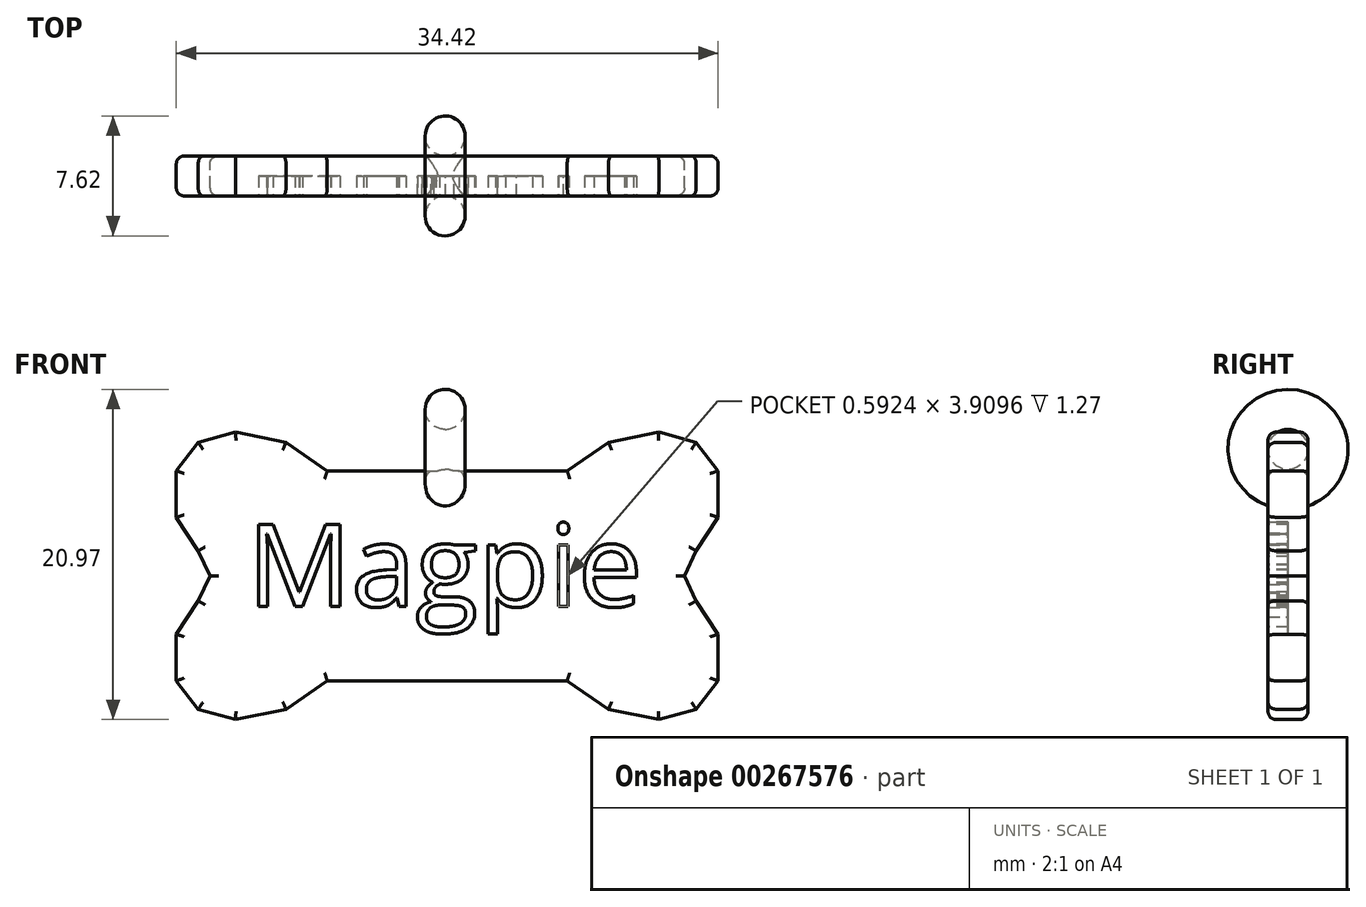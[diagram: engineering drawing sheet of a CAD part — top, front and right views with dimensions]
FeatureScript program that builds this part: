
annotation { "Feature Type Name" : "Feature", "Feature Type Description" : "" }
export const myFeature = defineFeature(function(context is Context, id is Id, definition is map)
    precondition{}
    {
        {
            var Q0;
            Q0=qCreatedBy(makeId("Front.planeOp"),FACE);
            var sketch = newSketch(context, id + "F0", { "sketchPlane" : qUnion([Q0])});
            skLineSegment(sketch, "E0", {"start": v(-5.6, 6.67) * mm, "end": v(2.01, 6.67) * mm});
            skLineSegment(sketch, "E1", {"start": v(2.01, 6.67) * mm, "end": v(4.63, 8.47) * mm});
            skLineSegment(sketch, "E2", {"start": v(4.63, 8.47) * mm, "end": v(7.83, 9.13) * mm});
            skLineSegment(sketch, "E3", {"start": v(7.83, 9.13) * mm, "end": v(10.2, 8.47) * mm});
            skLineSegment(sketch, "E4", {"start": v(10.2, 8.47) * mm, "end": v(11.6, 6.67) * mm});
            skLineSegment(sketch, "E5", {"start": v(11.6, 6.67) * mm, "end": v(11.6, 3.72) * mm});
            skLineSegment(sketch, "E6", {"start": v(11.6, 3.72) * mm, "end": v(10.2, 1.59) * mm});
            skLineSegment(sketch, "E7.MirrorCS", {"start": v(-5.6, 6.67) * mm, "end": v(-13.23, 6.67) * mm});
            skLineSegment(sketch, "E8.MirrorCS", {"start": v(-13.23, 6.67) * mm, "end": v(-15.85, 8.47) * mm});
            skLineSegment(sketch, "E9.MirrorCS", {"start": v(-15.85, 8.47) * mm, "end": v(-19.05, 9.13) * mm});
            skLineSegment(sketch, "E10.MirrorCS", {"start": v(-19.05, 9.13) * mm, "end": v(-21.42, 8.47) * mm});
            skLineSegment(sketch, "E11.MirrorCS", {"start": v(-21.42, 8.47) * mm, "end": v(-22.82, 6.67) * mm});
            skLineSegment(sketch, "E12.MirrorCS", {"start": v(-22.82, 6.67) * mm, "end": v(-22.82, 3.72) * mm});
            skLineSegment(sketch, "E13.MirrorCS", {"start": v(-22.82, 3.72) * mm, "end": v(-21.42, 1.59) * mm});
            skLineSegment(sketch, "E14.MirrorCS", {"start": v(11.6, -3.72) * mm, "end": v(10.2, -1.59) * mm});
            skLineSegment(sketch, "E15.MirrorCS", {"start": v(11.6, -6.67) * mm, "end": v(11.6, -3.72) * mm});
            skLineSegment(sketch, "E16.MirrorCS", {"start": v(10.2, -8.47) * mm, "end": v(11.6, -6.67) * mm});
            skLineSegment(sketch, "E17.MirrorCS", {"start": v(7.83, -9.13) * mm, "end": v(10.2, -8.47) * mm});
            skLineSegment(sketch, "E18.MirrorCS", {"start": v(4.63, -8.47) * mm, "end": v(7.83, -9.13) * mm});
            skLineSegment(sketch, "E19.MirrorCS", {"start": v(2.01, -6.67) * mm, "end": v(4.63, -8.47) * mm});
            skLineSegment(sketch, "E20.MirrorCS", {"start": v(-5.6, -6.67) * mm, "end": v(2.01, -6.67) * mm});
            skLineSegment(sketch, "E21.MirrorCS", {"start": v(-22.82, -3.72) * mm, "end": v(-21.42, -1.59) * mm});
            skLineSegment(sketch, "E22.MirrorCS", {"start": v(-22.82, -6.67) * mm, "end": v(-22.82, -3.72) * mm});
            skLineSegment(sketch, "E23.MirrorCS", {"start": v(-21.42, -8.47) * mm, "end": v(-22.82, -6.67) * mm});
            skLineSegment(sketch, "E24.MirrorCS", {"start": v(-19.05, -9.13) * mm, "end": v(-21.42, -8.47) * mm});
            skLineSegment(sketch, "E25.MirrorCS", {"start": v(-15.85, -8.47) * mm, "end": v(-19.05, -9.13) * mm});
            skLineSegment(sketch, "E26.MirrorCS", {"start": v(-13.23, -6.67) * mm, "end": v(-15.85, -8.47) * mm});
            skLineSegment(sketch, "E27.MirrorCS", {"start": v(-5.6, -6.67) * mm, "end": v(-13.23, -6.67) * mm});
            skLineSegment(sketch, "E28", {"start": v(10.2, 1.59) * mm, "end": v(9.47, 0) * mm});
            skLineSegment(sketch, "E29", {"start": v(9.47, 0) * mm, "end": v(10.2, -1.59) * mm});
            skLineSegment(sketch, "E30.MirrorCS", {"start": v(-21.42, 1.59) * mm, "end": v(-20.69, 0) * mm});
            skLineSegment(sketch, "E31.MirrorCS", {"start": v(-20.69, 0) * mm, "end": v(-21.42, -1.59) * mm});
            skSolve(sketch);
        }
        {
            var Q0;
            Q0 = qSketchRegion(id + "F0", true);
            extrude(context, id + "F1", {"entities" : qUnion([Q0]), "depth" : 2.54 * mm});
        }
        {
            var Q0;
            Q0=makeQuery(id+"F1.opExtrude","CAP_FACE",FACE,{"disambiguationData":[OSD([sQuery(id+"F0.wireOp",EDGE,"E0"),sQuery(id+"F0.wireOp",EDGE,"E1"),sQuery(id+"F0.wireOp",EDGE,"E2"),sQuery(id+"F0.wireOp",EDGE,"E3"),sQuery(id+"F0.wireOp",EDGE,"E4"),sQuery(id+"F0.wireOp",EDGE,"E5"),sQuery(id+"F0.wireOp",EDGE,"E6"),sQuery(id+"F0.wireOp",EDGE,"E7.MirrorCS"),sQuery(id+"F0.wireOp",EDGE,"E8.MirrorCS"),sQuery(id+"F0.wireOp",EDGE,"E9.MirrorCS"),sQuery(id+"F0.wireOp",EDGE,"E10.MirrorCS"),sQuery(id+"F0.wireOp",EDGE,"E11.MirrorCS"),sQuery(id+"F0.wireOp",EDGE,"E12.MirrorCS"),sQuery(id+"F0.wireOp",EDGE,"E13.MirrorCS"),sQuery(id+"F0.wireOp",EDGE,"E14.MirrorCS"),sQuery(id+"F0.wireOp",EDGE,"E15.MirrorCS"),sQuery(id+"F0.wireOp",EDGE,"E16.MirrorCS"),sQuery(id+"F0.wireOp",EDGE,"E17.MirrorCS"),sQuery(id+"F0.wireOp",EDGE,"E18.MirrorCS"),sQuery(id+"F0.wireOp",EDGE,"E19.MirrorCS"),sQuery(id+"F0.wireOp",EDGE,"E20.MirrorCS"),sQuery(id+"F0.wireOp",EDGE,"E21.MirrorCS"),sQuery(id+"F0.wireOp",EDGE,"E22.MirrorCS"),sQuery(id+"F0.wireOp",EDGE,"E23.MirrorCS"),sQuery(id+"F0.wireOp",EDGE,"E24.MirrorCS"),sQuery(id+"F0.wireOp",EDGE,"E25.MirrorCS"),sQuery(id+"F0.wireOp",EDGE,"E26.MirrorCS"),sQuery(id+"F0.wireOp",EDGE,"E27.MirrorCS"),sQuery(id+"F0.wireOp",EDGE,"E28"),sQuery(id+"F0.wireOp",EDGE,"E29"),sQuery(id+"F0.wireOp",EDGE,"E30.MirrorCS"),sQuery(id+"F0.wireOp",EDGE,"E31.MirrorCS")])],"isStart":false});
            var Q1;
            Q1=makeQuery(id+"F1.opExtrude","CAP_EDGE",EDGE,{"disambiguationData":[OSD([sQuery(id+"F0.wireOp",EDGE,"E0"),sQuery(id+"F0.wireOp",EDGE,"E7.MirrorCS")])],"isStart":false});
            var Q2;
            Q2=makeQuery(id+"F1.opExtrude","CAP_EDGE",EDGE,{"disambiguationData":[OSD([sQuery(id+"F0.wireOp",EDGE,"E31.MirrorCS")])],"isStart":false});
            var Q3;
            Q3=makeQuery(id+"F1.opExtrude","CAP_FACE",FACE,{"disambiguationData":[OSD([sQuery(id+"F0.wireOp",EDGE,"E0"),sQuery(id+"F0.wireOp",EDGE,"E1"),sQuery(id+"F0.wireOp",EDGE,"E2"),sQuery(id+"F0.wireOp",EDGE,"E3"),sQuery(id+"F0.wireOp",EDGE,"E4"),sQuery(id+"F0.wireOp",EDGE,"E5"),sQuery(id+"F0.wireOp",EDGE,"E6"),sQuery(id+"F0.wireOp",EDGE,"E7.MirrorCS"),sQuery(id+"F0.wireOp",EDGE,"E8.MirrorCS"),sQuery(id+"F0.wireOp",EDGE,"E9.MirrorCS"),sQuery(id+"F0.wireOp",EDGE,"E10.MirrorCS"),sQuery(id+"F0.wireOp",EDGE,"E11.MirrorCS"),sQuery(id+"F0.wireOp",EDGE,"E12.MirrorCS"),sQuery(id+"F0.wireOp",EDGE,"E13.MirrorCS"),sQuery(id+"F0.wireOp",EDGE,"E14.MirrorCS"),sQuery(id+"F0.wireOp",EDGE,"E15.MirrorCS"),sQuery(id+"F0.wireOp",EDGE,"E16.MirrorCS"),sQuery(id+"F0.wireOp",EDGE,"E17.MirrorCS"),sQuery(id+"F0.wireOp",EDGE,"E18.MirrorCS"),sQuery(id+"F0.wireOp",EDGE,"E19.MirrorCS"),sQuery(id+"F0.wireOp",EDGE,"E20.MirrorCS"),sQuery(id+"F0.wireOp",EDGE,"E21.MirrorCS"),sQuery(id+"F0.wireOp",EDGE,"E22.MirrorCS"),sQuery(id+"F0.wireOp",EDGE,"E23.MirrorCS"),sQuery(id+"F0.wireOp",EDGE,"E24.MirrorCS"),sQuery(id+"F0.wireOp",EDGE,"E25.MirrorCS"),sQuery(id+"F0.wireOp",EDGE,"E26.MirrorCS"),sQuery(id+"F0.wireOp",EDGE,"E27.MirrorCS"),sQuery(id+"F0.wireOp",EDGE,"E28"),sQuery(id+"F0.wireOp",EDGE,"E29"),sQuery(id+"F0.wireOp",EDGE,"E30.MirrorCS"),sQuery(id+"F0.wireOp",EDGE,"E31.MirrorCS")])],"isStart":true});
            fillet(context, id + "F2", {"entities" : qUnion([Q0, Q1, Q2, Q3]), "radius" : 0.5 * mm, "tangentPropagation" : true, "allowEdgeOverflow" : false});
        }
        {
            var Q0;
            Q0=makeQuery(id+"F1.opExtrude","CAP_FACE",FACE,{"disambiguationData":[OSD([sQuery(id+"F0.wireOp",EDGE,"E0"),sQuery(id+"F0.wireOp",EDGE,"E1"),sQuery(id+"F0.wireOp",EDGE,"E2"),sQuery(id+"F0.wireOp",EDGE,"E3"),sQuery(id+"F0.wireOp",EDGE,"E4"),sQuery(id+"F0.wireOp",EDGE,"E5"),sQuery(id+"F0.wireOp",EDGE,"E6"),sQuery(id+"F0.wireOp",EDGE,"E7.MirrorCS"),sQuery(id+"F0.wireOp",EDGE,"E8.MirrorCS"),sQuery(id+"F0.wireOp",EDGE,"E9.MirrorCS"),sQuery(id+"F0.wireOp",EDGE,"E10.MirrorCS"),sQuery(id+"F0.wireOp",EDGE,"E11.MirrorCS"),sQuery(id+"F0.wireOp",EDGE,"E12.MirrorCS"),sQuery(id+"F0.wireOp",EDGE,"E13.MirrorCS"),sQuery(id+"F0.wireOp",EDGE,"E14.MirrorCS"),sQuery(id+"F0.wireOp",EDGE,"E15.MirrorCS"),sQuery(id+"F0.wireOp",EDGE,"E16.MirrorCS"),sQuery(id+"F0.wireOp",EDGE,"E17.MirrorCS"),sQuery(id+"F0.wireOp",EDGE,"E18.MirrorCS"),sQuery(id+"F0.wireOp",EDGE,"E19.MirrorCS"),sQuery(id+"F0.wireOp",EDGE,"E20.MirrorCS"),sQuery(id+"F0.wireOp",EDGE,"E21.MirrorCS"),sQuery(id+"F0.wireOp",EDGE,"E22.MirrorCS"),sQuery(id+"F0.wireOp",EDGE,"E23.MirrorCS"),sQuery(id+"F0.wireOp",EDGE,"E24.MirrorCS"),sQuery(id+"F0.wireOp",EDGE,"E25.MirrorCS"),sQuery(id+"F0.wireOp",EDGE,"E26.MirrorCS"),sQuery(id+"F0.wireOp",EDGE,"E27.MirrorCS"),sQuery(id+"F0.wireOp",EDGE,"E28"),sQuery(id+"F0.wireOp",EDGE,"E29"),sQuery(id+"F0.wireOp",EDGE,"E30.MirrorCS"),sQuery(id+"F0.wireOp",EDGE,"E31.MirrorCS")])],"isStart":false});
            var sketch = newSketch(context, id + "F3", { "sketchPlane" : qUnion([Q0])});
            skText(sketch, "E32", { "text": "Magpie", "fontName": "OpenSans-Regular.ttf"});
            const initialGuessF3  = {"E32": [-0.0183, -0.00195, 1, 0, 0.00526]};
            skSetInitialGuess(sketch, initialGuessF3);
            skSolve(sketch);
        }
        {
            var Q0;
            Q0 = qSketchRegion(id + "F3", true);
            extrude(context, id + "F4", {"entities" : qUnion([Q0]), "operationType" : NewBodyOperationType.REMOVE, "oppositeDirection" : true, "depth" : 1.27 * mm});
        }
        {
            var Q0;
            Q0=qCreatedBy(makeId("Front.planeOp"),FACE);
            cPlane(context, id + "F5", {"entities" : qUnion([Q0]), "cplaneType" : CPlaneType.OFFSET, "offset" : 1.27 * mm, "width" : 152.4 * mm, "height" : 152.4 * mm});
        }
        {
            var Q0;
            Q0=qCreatedBy(id+"F5.planeOp",FACE);
            var sketch = newSketch(context, id + "F6", { "sketchPlane" : qUnion([Q0])});
            skCircle(sketch, "E33", {"center": v(-5.74, 5.5) * mm, "radius": 1.27 * mm});
            skLineSegment(sketch, "E34", {"start": v(-5.74, 5.5) * mm, "end": v(-5.74, 8.03) * mm});
            skLineSegment(sketch, "E35", {"start": v(-5.74, 8.03) * mm, "end": v(0.39, 8.03) * mm});
            skSolve(sketch);
        }
        {
            var Q0;
            Q0 = qSketchRegion(id + "F6", true);
            var Q1;
            Q1=sQuery(id+"F6.wireOp",EDGE,"E35");
            revolve(context, id + "F7", {"operationType" : NewBodyOperationType.ADD, "entities" : qUnion([Q0]), "axis" : qUnion([Q1]), "revolveType" : RevolveType.FULL});
        }
    });
